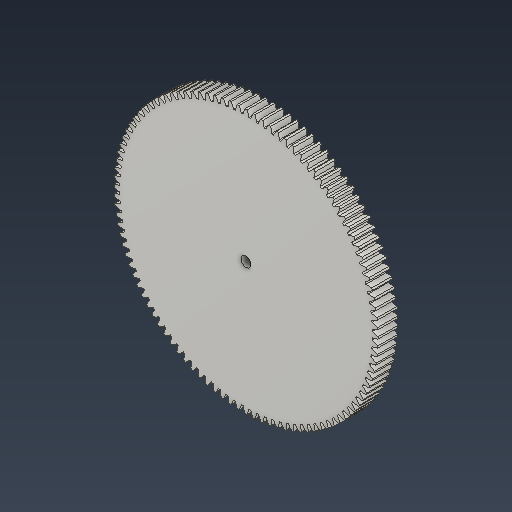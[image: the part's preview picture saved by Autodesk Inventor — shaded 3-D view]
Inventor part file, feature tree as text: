
AUTODESK INVENTOR PART (.ipt)
format: ipt  version: 2021 (Build 250183000, 183)  size: 568,832 bytes
history: native  units: mm (DEFAULTED — no unit token found)
features: plane x3, other x3, sketch x3, extrude x2
ambient origin geometry x8: Origin, YZ Plane, XZ Plane, XY Plane, X Axis, Y Axis, Z Axis, Center Point
bodies: Solid1 (feature_tree)
feature tree (11):
  extrude  "Extrusion1"  Depth=10.0mm TaperAngle=0.0deg
  plane  "Work Plane2"
  plane  "Work Plane8"
  plane  "Work Plane9"
  other  "Spur Gear"
  extrude  "Extrusion2"  Depth=10.0mm TaperAngle=0.0deg
  sketch  "Sketch1"  dims[d0=132.5mm d1=10.0mm d2=0.0mm]
  sketch  "Sketch2"  dims[d3=130.0mm d4=10.0mm d5=0.0mm]
  other  "Srf1"
  sketch  "Sketch3"  dims[d16=85.0mm d17=0.0mm d34=0.302076mm d39=0.0mm d41=0.0mm d43=85.0mm d46=85.0mm d47=0.0mm d48=0.0mm d49=5.0mm d50=0.0mm d51=0.0mm]
  other  "Pitch Diameter"
